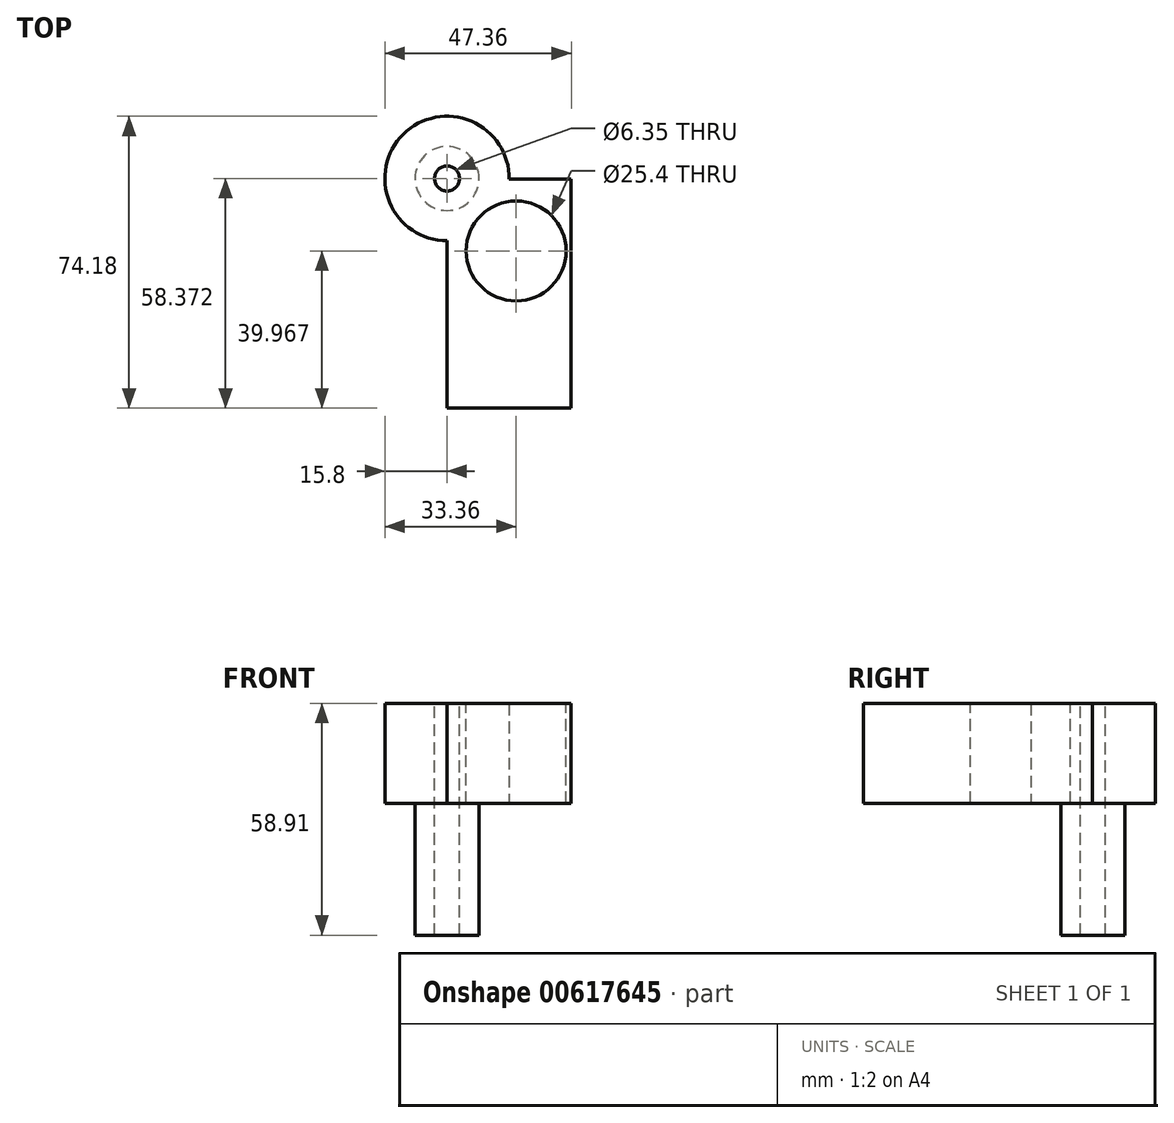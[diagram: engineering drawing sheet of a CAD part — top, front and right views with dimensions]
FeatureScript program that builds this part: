
annotation { "Feature Type Name" : "Feature", "Feature Type Description" : "" }
export const myFeature = defineFeature(function(context is Context, id is Id, definition is map)
    precondition{}
    {
        {
            var Q0;
            Q0=qCreatedBy(makeId("Top.planeOp"),FACE);
            var sketch = newSketch(context, id + "F0", { "sketchPlane" : qUnion([Q0])});
            skLineSegment(sketch, "E0.bottom", {"start": v(0, 0) * mm, "end": v(31.56, 0) * mm});
            skLineSegment(sketch, "E0.top", {"start": v(0, 33.18) * mm, "end": v(31.56, 33.18) * mm});
            skLineSegment(sketch, "E0.left", {"start": v(0, 0) * mm, "end": v(0, 33.18) * mm});
            skLineSegment(sketch, "E0.right", {"start": v(31.56, 0) * mm, "end": v(31.56, 33.18) * mm});
            skSolve(sketch);
        }
        {
            var Q0;
            Q0 = qSketchRegion(id + "F0", true);
            var sketch = newSketch(context, id + "F1", { "sketchPlane" : qUnion([Q0])});
            skCircle(sketch, "E1", {"center": v(0, 33.37) * mm, "radius": 15.8 * mm});
            skSolve(sketch);
        }
        {
            var Q0;
            Q0 = qSketchRegion(id + "F1", true);
            extrude(context, id + "F2", {"entities" : qUnion([Q0]), "depth" : 25.4 * mm, "offsetDistance" : 25.4 * mm});
        }
        {
            var Q0;
            Q0 = qSketchRegion(id + "F0", true);
            var Q1;
            Q1=makeQuery(id+"F0.imprint","IMPRINT",FACE,{"disambiguationData":[TD([[makeQuery(id+"F0.imprint","IMPRINT",EDGE,{"derivedFrom":sQuery(id+"F0.wireOp",EDGE,"E0.bottom")}),1.0]])]});
            extrude(context, id + "F3", {"entities" : qUnion([Q0, Q1]), "operationType" : NewBodyOperationType.ADD, "depth" : 25.4 * mm, "offsetDistance" : 25.4 * mm});
        }
        {
            var Q0;
            Q0=makeQuery(id+"F3.boolean.opBoolean","MERGE",FACE,{"derivedFrom":[makeQuery(id+"F2.opExtrude","CAP_FACE",FACE,{"disambiguationData":[OSD([sQuery(id+"F1.wireOp",EDGE,"E1")])],"isStart":false}),makeQuery(id+"F3.opExtrude","CAP_FACE",FACE,{"disambiguationData":[OSD([sQuery(id+"F0.wireOp",EDGE,"E0.bottom"),sQuery(id+"F0.wireOp",EDGE,"E0.top"),sQuery(id+"F0.wireOp",EDGE,"E0.left"),sQuery(id+"F0.wireOp",EDGE,"E0.right")])],"isStart":false})]});
            var sketch = newSketch(context, id + "F4", { "sketchPlane" : qUnion([Q0])});
            skCircle(sketch, "E2", {"center": v(0, 33.37) * mm, "radius": 8.13 * mm});
            skSolve(sketch);
        }
        {
            var Q0;
            Q0 = qSketchRegion(id + "F4", true);
            extrude(context, id + "F5", {"entities" : qUnion([Q0]), "operationType" : NewBodyOperationType.ADD, "oppositeDirection" : true, "depth" : 58.9 * mm, "offsetDistance" : 25.4 * mm});
        }
        {
            var Q0;
            Q0=makeQuery(id+"F3.boolean.opBoolean","MERGE",FACE,{"derivedFrom":[makeQuery(id+"F2.opExtrude","CAP_FACE",FACE,{"disambiguationData":[OSD([sQuery(id+"F1.wireOp",EDGE,"E1")])],"isStart":false}),makeQuery(id+"F3.opExtrude","CAP_FACE",FACE,{"disambiguationData":[OSD([sQuery(id+"F0.wireOp",EDGE,"E0.bottom"),sQuery(id+"F0.wireOp",EDGE,"E0.top"),sQuery(id+"F0.wireOp",EDGE,"E0.left"),sQuery(id+"F0.wireOp",EDGE,"E0.right")])],"isStart":false})]});
            var sketch = newSketch(context, id + "F6", { "sketchPlane" : qUnion([Q0])});
            skCircle(sketch, "E3", {"center": v(0, 33.37) * mm, "radius": 11.6 * mm});
            skSolve(sketch);
        }
        {
            var Q0;
            Q0=sQuery(id+"F6.wireOp",VERTEX,"E3.center");
            var Q1;
            Q1=makeQuery(id+"F2.opExtrude","SWEPT_BODY",BODY,{"disambiguationData":[OSD([sQuery(id+"F1.wireOp",EDGE,"E1")])]});
            hole(context, id + "F7", {"style" : HoleStyle.SIMPLE, "endStyle" : HoleEndStyle.THROUGH, "holeDiameter" : 6.35 * mm, "majorDiameter" : 6.35 * mm, "isTappedThrough" : true, "tappedDepth" : 12.7 * mm, "tapClearance" : 3, "locations" : qUnion([Q0]), "scope" : qUnion([Q1])});
        }
        {
            var Q0;
            Q0=makeQuery(id+"F3.boolean.opBoolean","MERGE",FACE,{"derivedFrom":[makeQuery(id+"F2.opExtrude","CAP_FACE",FACE,{"disambiguationData":[OSD([sQuery(id+"F1.wireOp",EDGE,"E1")])],"isStart":false}),makeQuery(id+"F3.opExtrude","CAP_FACE",FACE,{"disambiguationData":[OSD([sQuery(id+"F0.wireOp",EDGE,"E0.bottom"),sQuery(id+"F0.wireOp",EDGE,"E0.top"),sQuery(id+"F0.wireOp",EDGE,"E0.left"),sQuery(id+"F0.wireOp",EDGE,"E0.right")])],"isStart":false})]});
            var sketch = newSketch(context, id + "F8", { "sketchPlane" : qUnion([Q0])});
            skPoint(sketch, "E4", {"position": v(17.56, 14.97) * mm});
            skSolve(sketch);
        }
        {
            var Q0;
            Q0=sQuery(id+"F8.wireOp",VERTEX,"E4");
            var Q1;
            Q1=makeQuery(id+"F2.opExtrude","SWEPT_BODY",BODY,{"disambiguationData":[OSD([sQuery(id+"F1.wireOp",EDGE,"E1")])]});
            hole(context, id + "F9", {"style" : HoleStyle.SIMPLE, "endStyle" : HoleEndStyle.THROUGH, "holeDiameter" : 25.4 * mm, "majorDiameter" : 6.35 * mm, "isTappedThrough" : true, "tappedDepth" : 12.7 * mm, "tapClearance" : 3, "locations" : qUnion([Q0]), "scope" : qUnion([Q1])});
        }
        {
            var Q0;
            Q0=makeQuery(id+"F3.boolean.opBoolean","MERGE",FACE,{"derivedFrom":[makeQuery(id+"F2.opExtrude","CAP_FACE",FACE,{"disambiguationData":[OSD([sQuery(id+"F1.wireOp",EDGE,"E1")])],"isStart":false}),makeQuery(id+"F3.opExtrude","CAP_FACE",FACE,{"disambiguationData":[OSD([sQuery(id+"F0.wireOp",EDGE,"E0.bottom"),sQuery(id+"F0.wireOp",EDGE,"E0.top"),sQuery(id+"F0.wireOp",EDGE,"E0.left"),sQuery(id+"F0.wireOp",EDGE,"E0.right")])],"isStart":false})]});
            var sketch = newSketch(context, id + "F10", { "sketchPlane" : qUnion([Q0])});
            skCircle(sketch, "E5", {"center": v(17.56, 14.97) * mm, "radius": 9.24 * mm});
            skSolve(sketch);
        }
        {
            var Q0;
            Q0=makeQuery(id+"F10.imprint","IMPRINT",FACE,{"disambiguationData":[TD([[makeQuery(id+"F10.imprint","IMPRINT",EDGE,{"derivedFrom":makeQuery(id+"F3.opExtrude","CAP_EDGE",EDGE,{"disambiguationData":[OSD([sQuery(id+"F0.wireOp",EDGE,"E0.bottom")])],"isStart":false})}),1.0]])]});
            var sketch = newSketch(context, id + "F11", { "sketchPlane" : qUnion([Q0])});
            skLineSegment(sketch, "E6", {"start": v(30.9, 49.1) * mm, "end": v(-11.73, 60.17) * mm});
            skSolve(sketch);
        }
        {
            var Q0;
            Q0=qCreatedBy(makeId("Top.planeOp"),FACE);
            var sketch = newSketch(context, id + "F12", { "sketchPlane" : qUnion([Q0])});
            skLineSegment(sketch, "E7", {"start": v(25.45, 57.25) * mm, "end": v(6.84, 57.25) * mm, "construction": true});
            skSolve(sketch);
        }
        {
            var Q0;
            Q0=sQuery(id+"F10.wireOp",EDGE,"E5");
            var Q1;
            Q1=sQuery(id+"F12.wireOp",EDGE,"E7");
            revolve(context, id + "F13", {"bodyType" : ToolBodyType.SURFACE, "surfaceEntities" : qUnion([Q0]), "axis" : qUnion([Q1]), "revolveType" : RevolveType.FULL});
        }
        {
            var Q0;
            Q0=makeQuery(id+"F3.opExtrude","SWEPT_FACE",FACE,{"disambiguationData":[OSD([sQuery(id+"F0.wireOp",EDGE,"E0.bottom")])]});
            extrude(context, id + "F14", {"entities" : qUnion([Q0]), "operationType" : NewBodyOperationType.ADD, "depth" : 25 * mm, "offsetDistance" : 25 * mm});
        }
    });
